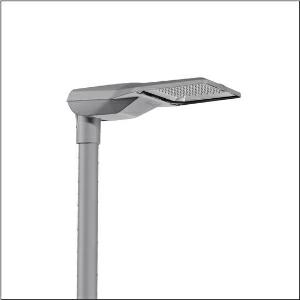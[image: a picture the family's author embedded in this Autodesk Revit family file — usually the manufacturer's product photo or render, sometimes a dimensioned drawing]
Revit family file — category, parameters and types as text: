
# Revit family: streetlight_sl_21_iq_midi___pl52_5xe3h31g08mb_961f
name_source: partatom
category: Lighting Fixtures
units: mm (PartAtom-declared; Revit-internal decimal feet)

## family parameters
Cut with Voids When Loaded = No
Host = Face
Light Source = No
Part Type = Normal
Room Calculation Point = No
Round Connector Dimension = Use Diameter
Shared = No

## types (1)
- --- (1 x LED, 19170 lm, 146.7 W, 3000K)
    Apparent Load = 147 VA
    CIE Flux Codes = 27 59 98 100 100
    Color Rendering = 70
    Color Temperature = 3000K
    Default Elevation = 1800 mm
    Description = Streetlight SL 21 iQ midi, mast luminaire, primary light control with lens, of PMMA, primary optical cover: cover, of toughened safety glass, transparent, light distribution: PL52, light emission: direct distribution, primary light characteristic: asymmetric, installation type: post-top, side-entry, LED, High Power LED, rated luminous flux: 19.170lm, luminous efficacy: 131lm/W, light colour: 730, colour temperature: 3000K, control gear: iQ Street-Remote, control: Street-Remote, Auto-Match, Temp-Guard, Lumen-Switch, Night-Set, Smart-Wire, Light-Fading, Desk-Remote (wireless, voltage-free reading and setting of iQ features in the workshop via application-optimized NFC function/RFID function), optimised constant luminous flux control (CLO 2.0), pre-setting: linear dimming characteristic, mains connection: 230..240V, AC, 50/60Hz, start of lifetime: 147W, end of service life: 161W, reduction: 62W, luminaire housing, of diecast aluminium, powder-coated, Siteco® metallic grey (DB 702S), corrosivity category C5 high according to DIN EN ISO 12944, please order mast flange separately, inclination adjustable: 0°, 5°, 10°, 15°, sealing non-destructively replaceable, multi-level sealing system, length: 644mm, width: 335mm, height: 110mm, mast flange for spigot size: 42mm (side-entry): 5XC10008XM4, 60/48mm (side-entry/post-top): 5XC10108XM2, 76/60mm (side-entry/post-top): 5XC10108XM1, mounting height: 4..8m, protection rating (complete): IP66, insulation class (complete): insulation class II (safety insulation), certification: CE, ENEC, ENEC+, VDE, impact resistance: IK10, permissible operating ambient temperature for outdoor applications: -40..+50°C, standard-compliant lighting for roads and squares, packaging unit: 1 piece

Light Distribution: PL52
    Height = 111 mm
    Lamp = 1 x LED
    Lamp Light Flux = 19170 lm
    Lamp Power = 146.7 W
    Lamp count = 1
    Length = 644 mm
    Luminous efficacy = 131 lm/W
    Manufacturer = Siteco
    ModVariant = No
    Model = 5XE3H31G08MB
    Number of Poles = 1
    OnlyDefault = Yes
    Power Factor = 1
    Product Name = Streetlight SL 21 iQ midi | PL52
    Product group = mast luminaire | pylon top
    ProductGroupID = 6100
    Protection Class = Protection class II
    Protection Degree = IP 66
    RLX_Detail_Level = 1
    RLX_Emergency_Light_Flux = 0 lm
    RLX_Emergency_Type = 0
    RLX_Emergency_Type_DB = No
    RlxData = <blob elided: 36529 chars, md5=a45333d5>
    Socket = socket
    Standby Power = 0 W
    System Light Flux = 19169 lm
    System Power = 147 W
    Type Comments = factory setting: luminous flux: 100 % | dim-lin: 254 | 753 mA
    Type Image = l_1004298.jpg
    URL = http://relux.com
    VarID = @adj_192025
    Voltage = 0 V
    Weight = 0.00 kg
    Width = 336 mm

## geometry (parser evidence)
native form markers: Blend x4, Sweep x10
no freeform markers — native parametric forms only
